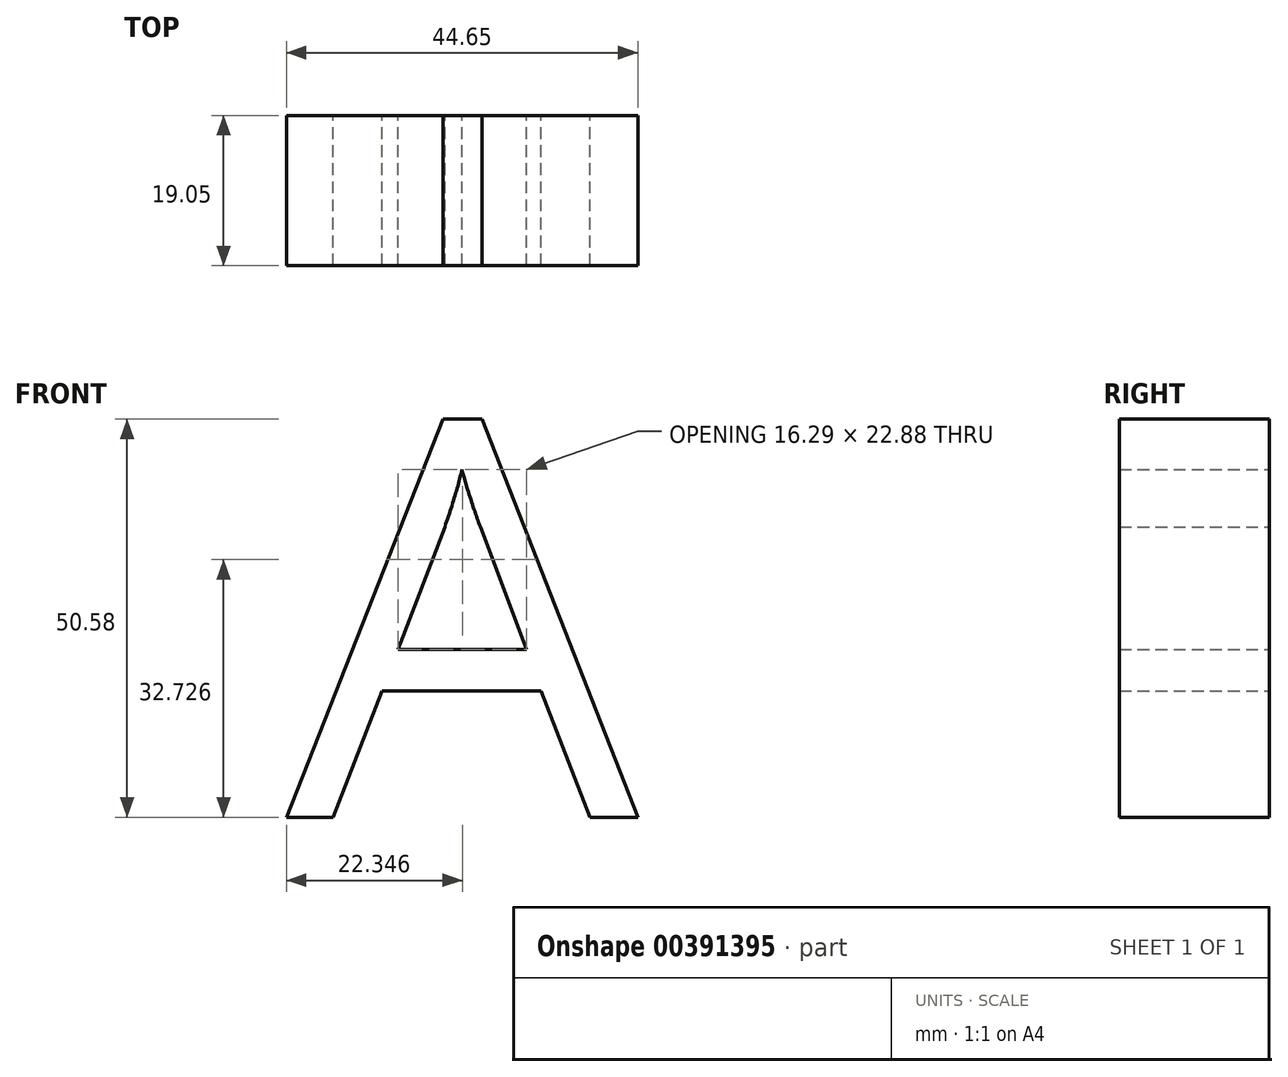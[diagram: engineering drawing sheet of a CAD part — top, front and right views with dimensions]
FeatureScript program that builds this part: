
annotation { "Feature Type Name" : "Feature", "Feature Type Description" : "" }
export const myFeature = defineFeature(function(context is Context, id is Id, definition is map)
    precondition{}
    {
        {
            var Q0;
            Q0=qCreatedBy(makeId("Front.planeOp"),FACE);
            var sketch = newSketch(context, id + "F0", { "sketchPlane" : qUnion([Q0])});
            skText(sketch, "E0", { "text": "A", "fontName": "OpenSans-Regular.ttf"});
            const initialGuessF0  = {"E0": [0, 0, 1, 0, 0.0508]};
            skSetInitialGuess(sketch, initialGuessF0);
            skSolve(sketch);
        }
        {
            var Q0;
            Q0 = qSketchRegion(id + "F0", true);
            extrude(context, id + "F1", {"entities" : qUnion([Q0]), "depth" : 19.05 * mm});
        }
    });
